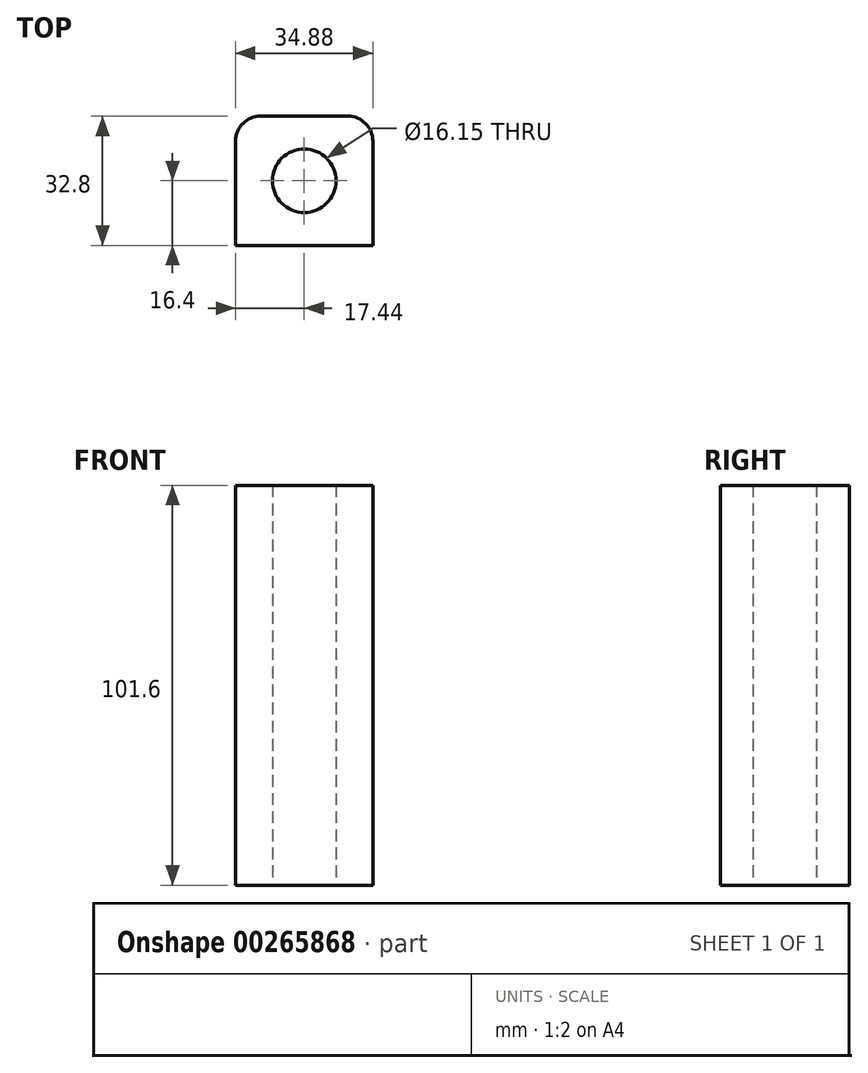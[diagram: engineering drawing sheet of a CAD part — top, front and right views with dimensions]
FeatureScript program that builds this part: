
annotation { "Feature Type Name" : "Feature", "Feature Type Description" : "" }
export const myFeature = defineFeature(function(context is Context, id is Id, definition is map)
    precondition{}
    {
        {
            var Q0;
            Q0=qCreatedBy(makeId("Top.planeOp"),FACE);
            var sketch = newSketch(context, id + "F0", { "sketchPlane" : qUnion([Q0])});
            skLineSegment(sketch, "E0.bottom", {"start": v(17.44, -16.4) * mm, "end": v(-17.44, -16.4) * mm});
            skLineSegment(sketch, "E0.top", {"start": v(17.44, 16.4) * mm, "end": v(-17.44, 16.4) * mm});
            skLineSegment(sketch, "E0.left", {"start": v(17.44, -16.4) * mm, "end": v(17.44, 16.4) * mm});
            skLineSegment(sketch, "E0.right", {"start": v(-17.44, -16.4) * mm, "end": v(-17.44, 16.4) * mm});
            skPoint(sketch, "E0.middle", {"position": v(0, 0) * mm});
            skCircle(sketch, "E1", {"center": v(0, 0) * mm, "radius": 8.08 * mm});
            skSolve(sketch);
        }
        {
            var Q0;
            Q0 = qSketchRegion(id + "F0", true);
            extrude(context, id + "F1", {"entities" : qUnion([Q0]), "depth" : 101.6 * mm});
        }
        {
            var Q0;
            Q0=makeQuery(id+"F1.opExtrude","SWEPT_EDGE",EDGE,{"disambiguationData":[OSD([sQuery(id+"F0.wireOp",EDGE,"E0.top"),sQuery(id+"F0.wireOp",EDGE,"E0.right")])]});
            var Q1;
            Q1=makeQuery(id+"F1.opExtrude","SWEPT_EDGE",EDGE,{"disambiguationData":[OSD([sQuery(id+"F0.wireOp",EDGE,"E0.top"),sQuery(id+"F0.wireOp",EDGE,"E0.left")])]});
            fillet(context, id + "F2", {"entities" : qUnion([Q0, Q1]), "radius" : 6.35 * mm, "tangentPropagation" : true, "allowEdgeOverflow" : false});
        }
    });
